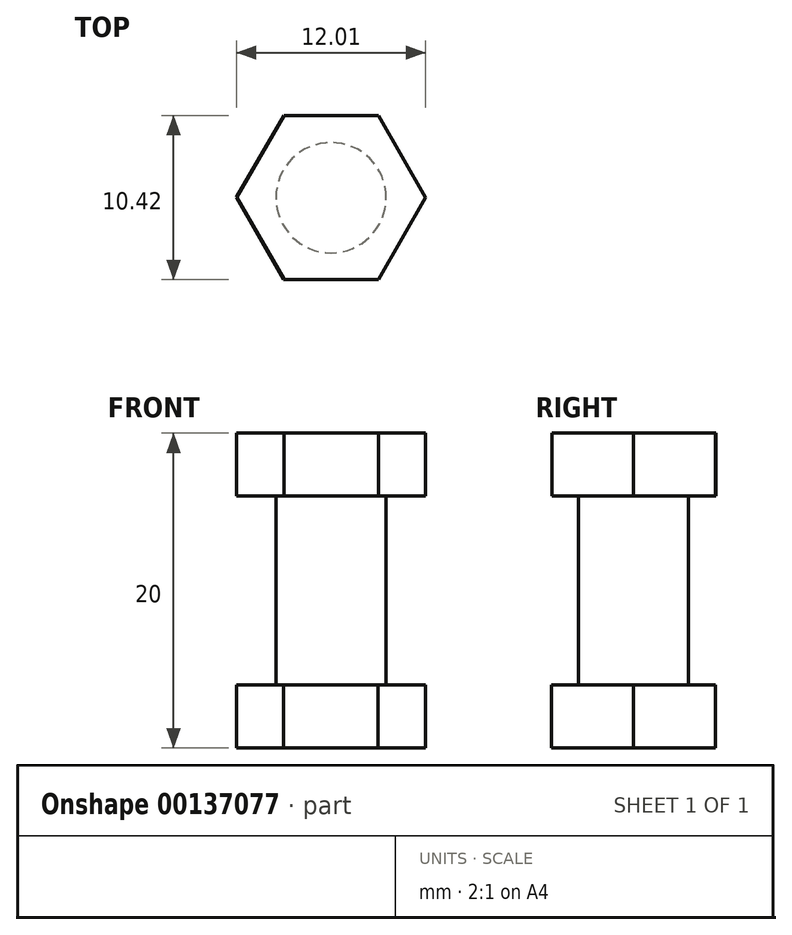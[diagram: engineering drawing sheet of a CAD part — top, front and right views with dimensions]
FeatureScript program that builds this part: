
annotation { "Feature Type Name" : "Feature", "Feature Type Description" : "" }
export const myFeature = defineFeature(function(context is Context, id is Id, definition is map)
    precondition{}
    {
        {
            var Q0;
            Q0=qCreatedBy(makeId("Top.planeOp"),FACE);
            var sketch = newSketch(context, id + "F0", { "sketchPlane" : qUnion([Q0])});
            skLineSegment(sketch, "E0.0", {"start": v(6, -0.01) * mm, "end": v(2.99, -5.2) * mm});
            skLineSegment(sketch, "E0.1", {"start": v(2.99, -5.2) * mm, "end": v(-3.01, -5.19) * mm});
            skLineSegment(sketch, "E0.2", {"start": v(-3.01, -5.19) * mm, "end": v(-6, 0.01) * mm});
            skLineSegment(sketch, "E0.3", {"start": v(-6, 0.01) * mm, "end": v(-2.99, 5.2) * mm});
            skLineSegment(sketch, "E0.4", {"start": v(-2.99, 5.2) * mm, "end": v(3.01, 5.19) * mm});
            skLineSegment(sketch, "E0.5", {"start": v(3.01, 5.19) * mm, "end": v(6, -0.01) * mm});
            skPoint(sketch, "E0.0.midPoint", {"position": v(4.5, -2.6) * mm});
            skSolve(sketch);
        }
        {
            var Q0;
            Q0 = qSketchRegion(id + "F0", true);
            extrude(context, id + "F1", {"entities" : qUnion([Q0]), "depth" : 4 * mm});
        }
        {
            var Q0;
            Q0=makeQuery(id+"F1.opExtrude","CAP_FACE",FACE,{"disambiguationData":[OSD([sQuery(id+"F0.wireOp",EDGE,"E0.0"),sQuery(id+"F0.wireOp",EDGE,"E0.1"),sQuery(id+"F0.wireOp",EDGE,"E0.2"),sQuery(id+"F0.wireOp",EDGE,"E0.3"),sQuery(id+"F0.wireOp",EDGE,"E0.4"),sQuery(id+"F0.wireOp",EDGE,"E0.5")])],"isStart":false});
            var sketch = newSketch(context, id + "F2", { "sketchPlane" : qUnion([Q0])});
            skCircle(sketch, "E1", {"center": v(0, 0) * mm, "radius": 3.5 * mm});
            skLineSegment(sketch, "E2", {"start": v(0, 3.5) * mm, "end": v(0, -3.5) * mm, "construction": true});
            skSolve(sketch);
        }
        {
            var Q0;
            Q0=makeQuery(id+"F2.imprint","IMPRINT",FACE,{"disambiguationData":[TD([[makeQuery(id+"F2.imprint","IMPRINT",EDGE,{"derivedFrom":sQuery(id+"F2.wireOp",EDGE,"E1")}),1.0]])]});
            extrude(context, id + "F3", {"entities" : qUnion([Q0]), "operationType" : NewBodyOperationType.ADD, "depth" : 12 * mm});
        }
        {
            var Q0;
            Q0=makeQuery(id+"F3.opExtrude","CAP_FACE",FACE,{"disambiguationData":[OSD([sQuery(id+"F2.wireOp",EDGE,"E1")])],"isStart":false});
            var sketch = newSketch(context, id + "F4", { "sketchPlane" : qUnion([Q0])});
            skLineSegment(sketch, "E3.0", {"start": v(6.01, 0) * mm, "end": v(3, -5.18) * mm});
            skLineSegment(sketch, "E3.1", {"start": v(3, -5.18) * mm, "end": v(-3, -5.17) * mm});
            skLineSegment(sketch, "E3.2", {"start": v(-3, -5.17) * mm, "end": v(-5.99, 0.04) * mm});
            skLineSegment(sketch, "E3.3", {"start": v(-5.99, 0.04) * mm, "end": v(-2.98, 5.22) * mm});
            skLineSegment(sketch, "E3.4", {"start": v(-2.98, 5.22) * mm, "end": v(3.02, 5.21) * mm});
            skLineSegment(sketch, "E3.5", {"start": v(3.02, 5.21) * mm, "end": v(6.01, 0) * mm});
            skPoint(sketch, "E3.0.midPoint", {"position": v(4.5, -2.59) * mm});
            skSolve(sketch);
        }
        {
            var Q0;
            Q0=makeQuery(id+"F4.imprint","IMPRINT",FACE,{"disambiguationData":[TD([[makeQuery(id+"F4.imprint","IMPRINT",EDGE,{"derivedFrom":sQuery(id+"F4.wireOp",EDGE,"E3.0")}),-1.0]])]});
            var Q1;
            Q1=makeQuery(id+"F4.imprint","IMPRINT",FACE,{"disambiguationData":[TD([[makeQuery(id+"F4.imprint","IMPRINT",EDGE,{"derivedFrom":makeQuery(id+"F3.opExtrude","CAP_EDGE",EDGE,{"disambiguationData":[OSD([sQuery(id+"F2.wireOp",EDGE,"E1")])],"isStart":false})}),1.0]])]});
            extrude(context, id + "F5", {"entities" : qUnion([Q0, Q1]), "operationType" : NewBodyOperationType.ADD, "depth" : 4 * mm});
        }
    });
